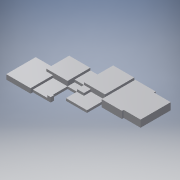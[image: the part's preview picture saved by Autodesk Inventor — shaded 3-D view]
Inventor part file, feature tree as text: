
AUTODESK INVENTOR PART (.ipt)
format: ipt  version: 2018.3 (Build 223284000, 284)  size: 218,624 bytes
history: native  units: mm
features: extrude x13, sketch x13
ambient origin geometry x8: Origin, YZ Plane, XZ Plane, XY Plane, X Axis, Y Axis, Z Axis, Center Point
bodies: Solid1 (feature_tree)
feature tree (26):
  extrude  "Extrusion1"  Depth=44.9mm
  extrude  "Extrusion2"  Depth=2.33mm
  extrude  "Extrusion3"  Depth=32.05mm
  extrude  "Extrusion4"  Depth=31.18mm TaperAngle=0.0deg
  extrude  "Extrusion5"  Depth=6.86mm TaperAngle=0.0deg
  extrude  "Extrusion6"  Depth=24.01mm TaperAngle=0.0deg
  extrude  "Extrusion7"  Depth=9.35mm
  extrude  "Extrusion8"  Depth=27.44mm
  extrude  "Extrusion9"  Depth=6.24mm
  extrude  "Extrusion10"  Depth=6.24mm TaperAngle=0.0deg
  extrude  "Extrusion11"  Depth=39.29mm
  extrude  "Extrusion12"  Depth=8.73mm TaperAngle=0.0deg
  extrude  "Extrusion13"  Depth=19.33mm TaperAngle=0.0deg
  sketch  "Sketch1"  dims[d0=49.58mm d1=44.9mm]
  sketch  "Sketch2"  dims[d2=22.45mm d3=2.33mm]
  sketch  "Sketch3"  dims[d4=9.35mm d5=0.0mm d6=32.05mm]
  sketch  "Sketch4"  dims[d7=5.16mm d8=31.18mm d9=0.0mm]
  sketch  "Sketch5"  dims[d10=3.12mm d11=0.0mm d12=6.86mm d13=0.0mm]
  sketch  "Sketch6"  dims[d14=3.12mm d15=24.01mm d16=0.0mm]
  sketch  "Sketch7"  dims[d17=9.35mm d18=9.35mm]
  sketch  "Sketch8"  dims[d19=3.12mm d20=0.0mm d21=27.44mm]
  sketch  "Sketch9"  dims[d22=12.47mm d23=0.0mm d24=6.24mm]
  sketch  "Sketch10"  dims[d25=3.12mm d26=6.24mm d27=0.0mm]
  sketch  "Sketch11"  dims[d28=28.06mm d29=0.0mm d30=39.29mm]
  sketch  "Sketch12"  dims[d31=23.7mm d32=0.0mm d33=8.73mm d34=0.0mm]
  sketch  "Sketch13"  dims[d35=26.82mm d36=19.33mm d37=0.0mm d38=6.24mm d39=4.37mm d40=4.37mm d41=0.0mm]
